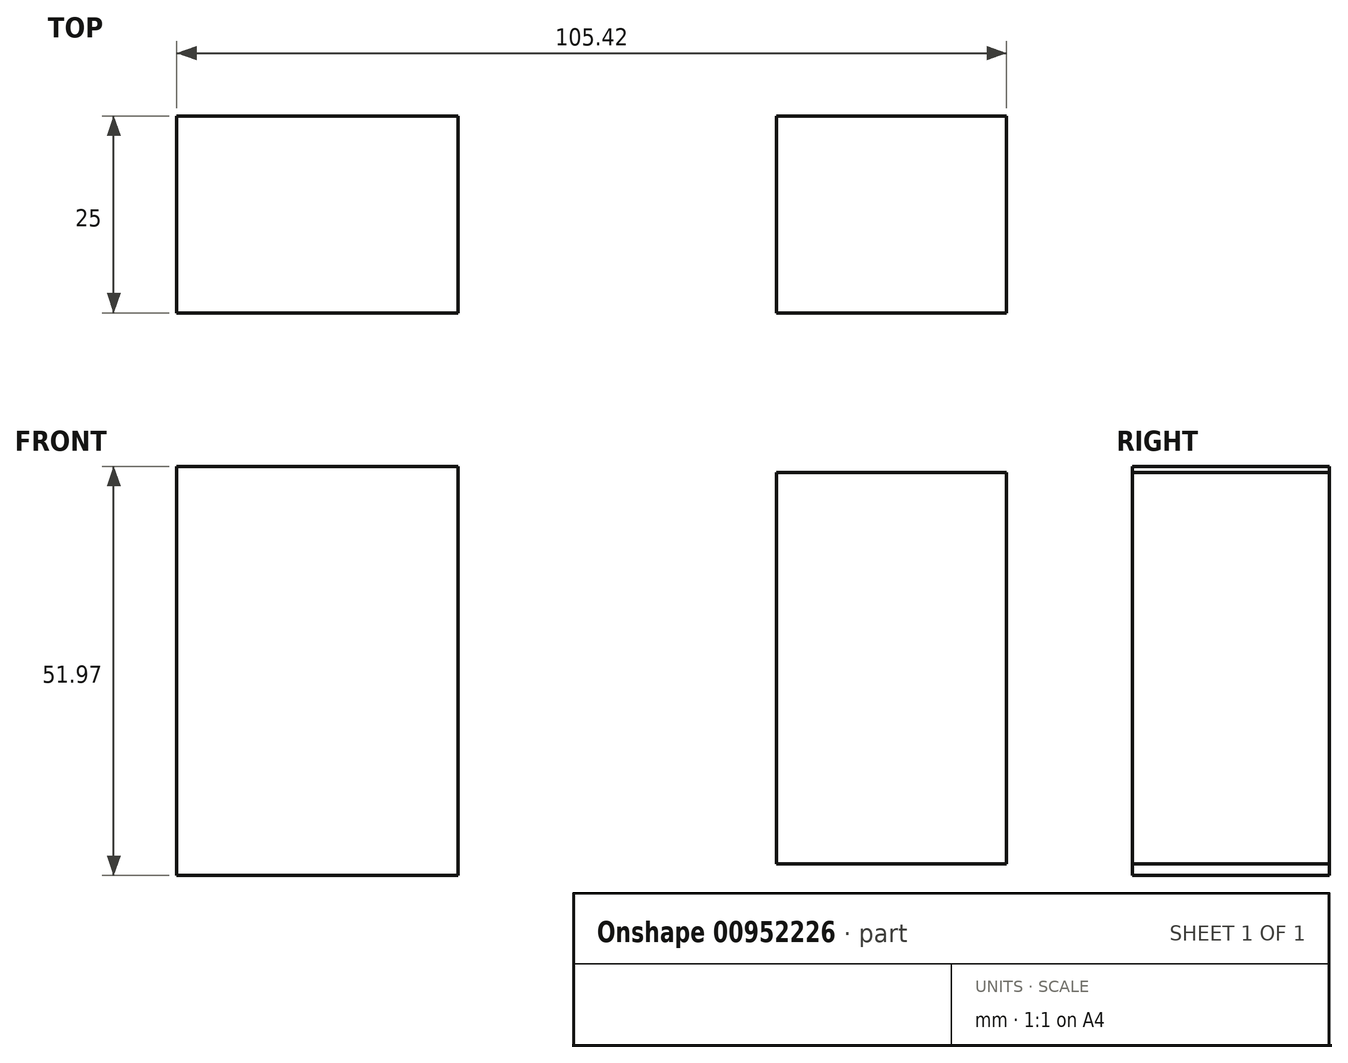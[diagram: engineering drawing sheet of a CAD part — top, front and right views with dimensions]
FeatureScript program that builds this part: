
annotation { "Feature Type Name" : "Feature", "Feature Type Description" : "" }
export const myFeature = defineFeature(function(context is Context, id is Id, definition is map)
    precondition{}
    {
        {
            var Q0;
            Q0=qCreatedBy(makeId("Front.planeOp"),FACE);
            var sketch = newSketch(context, id + "F0", { "sketchPlane" : qUnion([Q0])});
            skLineSegment(sketch, "E0.bottom", {"start": v(-19.32, 33.34) * mm, "end": v(16.4, 33.34) * mm});
            skLineSegment(sketch, "E0.top", {"start": v(-19.32, -18.63) * mm, "end": v(16.4, -18.63) * mm});
            skLineSegment(sketch, "E0.left", {"start": v(-19.32, 33.34) * mm, "end": v(-19.32, -18.63) * mm});
            skLineSegment(sketch, "E0.right", {"start": v(16.4, 33.34) * mm, "end": v(16.4, -18.63) * mm});
            skLineSegment(sketch, "E1.bottom", {"start": v(56.87, 32.56) * mm, "end": v(86.1, 32.56) * mm});
            skLineSegment(sketch, "E1.top", {"start": v(56.87, -17.17) * mm, "end": v(86.1, -17.17) * mm});
            skLineSegment(sketch, "E1.left", {"start": v(56.87, 32.56) * mm, "end": v(56.87, -17.17) * mm});
            skLineSegment(sketch, "E1.right", {"start": v(86.1, 32.56) * mm, "end": v(86.1, -17.17) * mm});
            skSolve(sketch);
        }
        {
            var Q0;
            Q0 = qSketchRegion(id + "F0", true);
            extrude(context, id + "F1", {"entities" : qUnion([Q0]), "depth" : 25 * mm, "offsetDistance" : 25 * mm});
        }
    });
